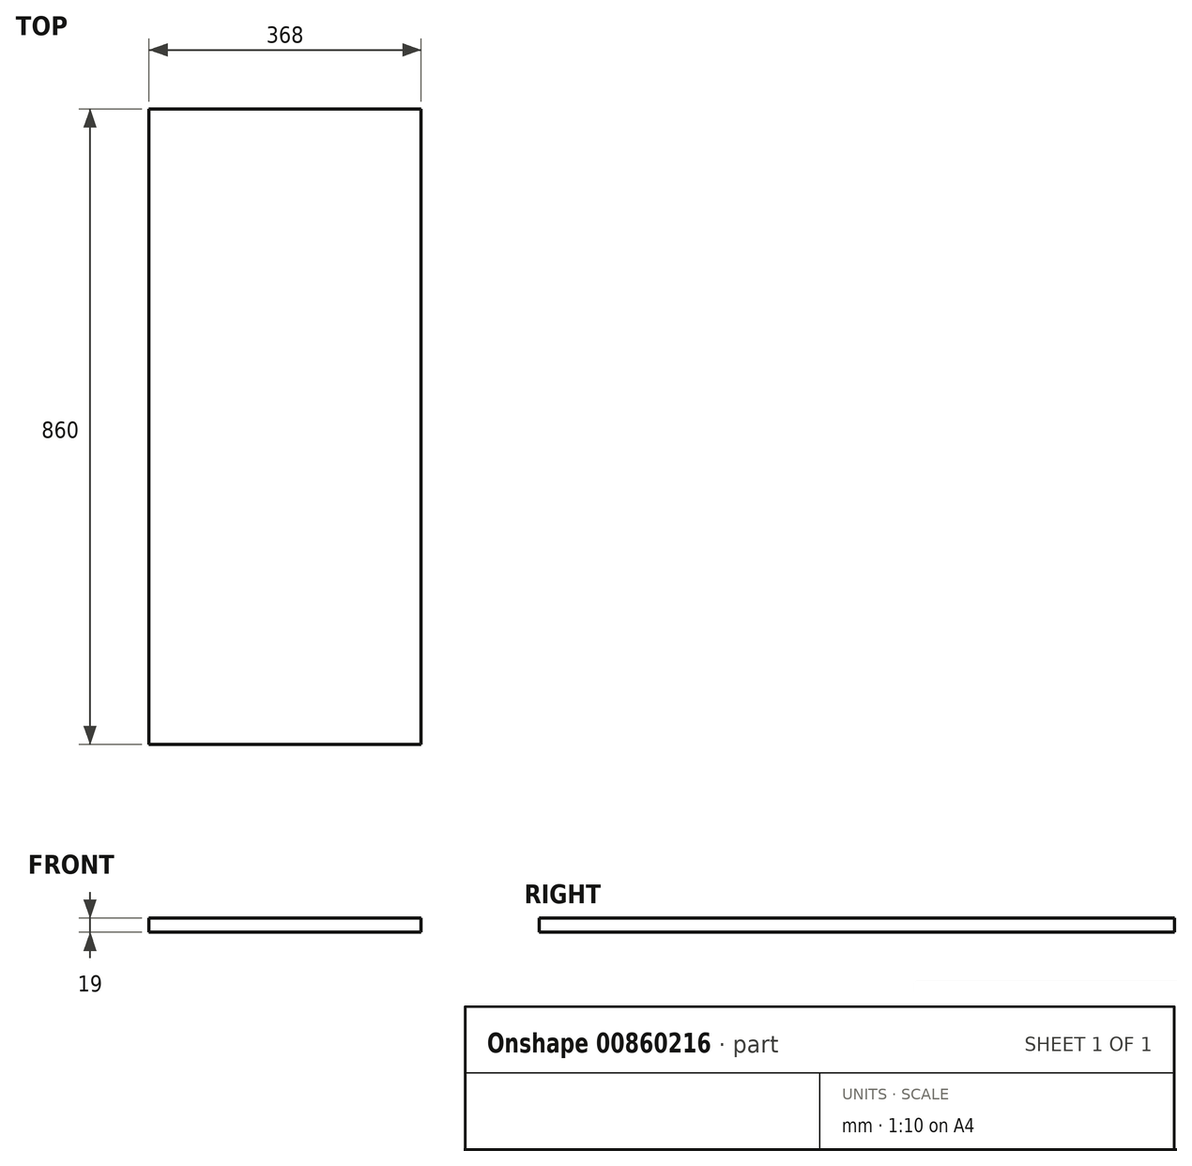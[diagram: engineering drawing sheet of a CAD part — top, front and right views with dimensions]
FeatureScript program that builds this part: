
annotation { "Feature Type Name" : "Feature", "Feature Type Description" : "" }
export const myFeature = defineFeature(function(context is Context, id is Id, definition is map)
    precondition{}
    {
        {
            var Q0;
            Q0=qCreatedBy(makeId("Front.planeOp"),FACE);
            var sketch = newSketch(context, id + "F0", { "sketchPlane" : qUnion([Q0])});
            skLineSegment(sketch, "E0.bottom", {"start": v(0, 0) * mm, "end": v(368, 0) * mm});
            skLineSegment(sketch, "E0.top", {"start": v(0, 19) * mm, "end": v(368, 19) * mm});
            skLineSegment(sketch, "E0.left", {"start": v(0, 0) * mm, "end": v(0, 19) * mm});
            skLineSegment(sketch, "E0.right", {"start": v(368, 0) * mm, "end": v(368, 19) * mm});
            skSolve(sketch);
        }
        {
            var Q0;
            Q0 = qSketchRegion(id + "F0", true);
            extrude(context, id + "F1", {"entities" : qUnion([Q0]), "depth" : 860 * mm, "offsetDistance" : 25 * mm});
        }
    });
